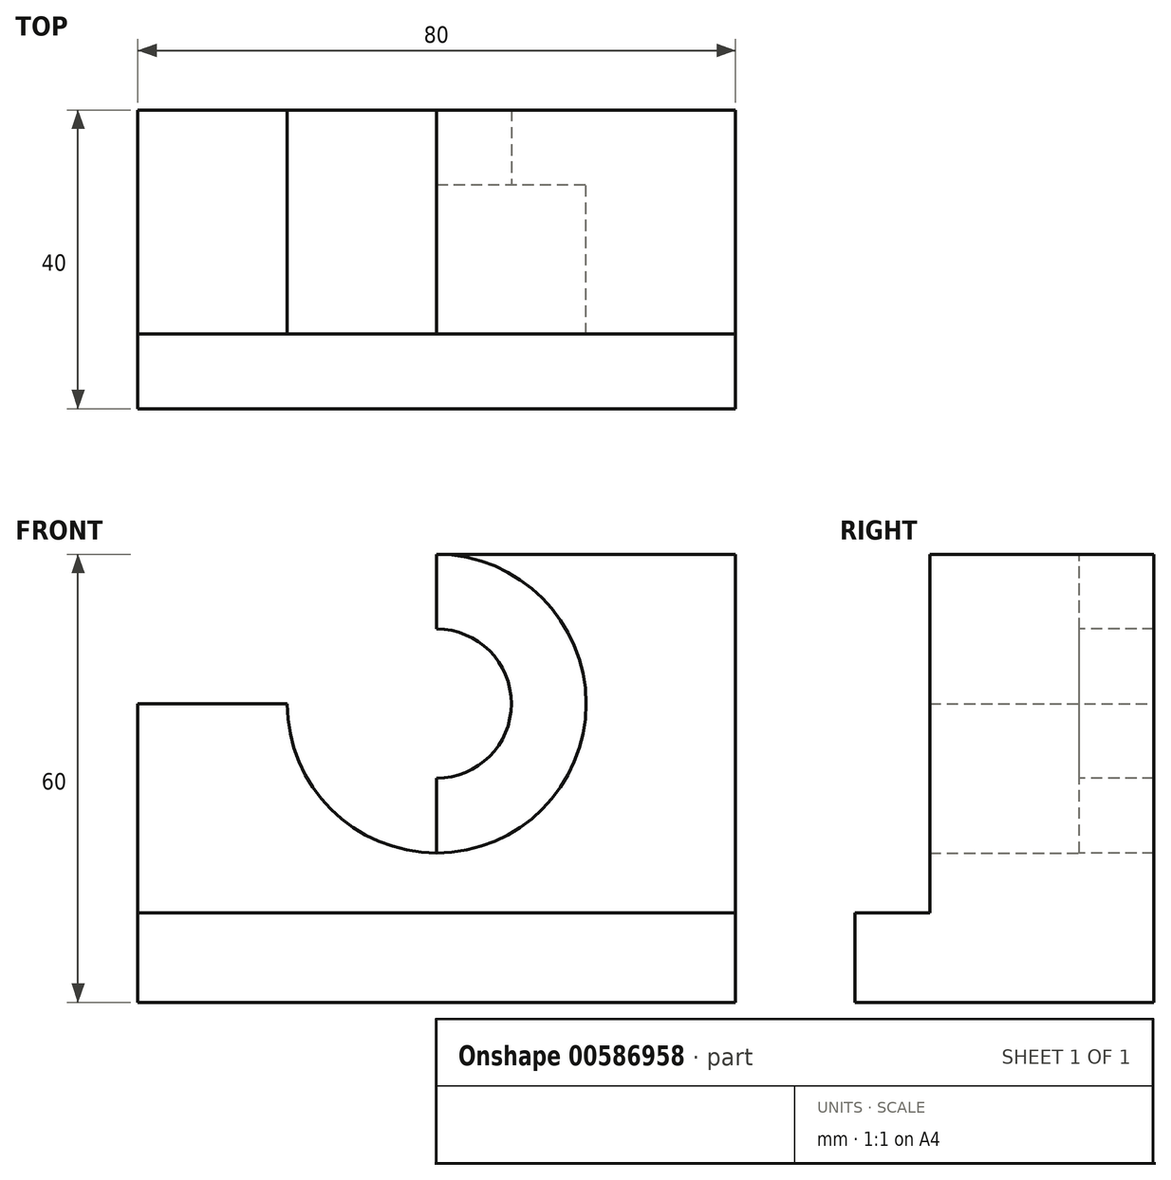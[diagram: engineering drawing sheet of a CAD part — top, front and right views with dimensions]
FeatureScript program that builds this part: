
annotation { "Feature Type Name" : "Feature", "Feature Type Description" : "" }
export const myFeature = defineFeature(function(context is Context, id is Id, definition is map)
    precondition{}
    {
        {
            var Q0;
            Q0=qCreatedBy(makeId("Top.planeOp"),FACE);
            var sketch = newSketch(context, id + "F0", { "sketchPlane" : qUnion([Q0])});
            skLineSegment(sketch, "E0.bottom", {"start": v(-24.56, -1) * mm, "end": v(55.44, -1) * mm});
            skLineSegment(sketch, "E0.top", {"start": v(-24.56, -41) * mm, "end": v(55.44, -41) * mm});
            skLineSegment(sketch, "E0.left", {"start": v(-24.56, -1) * mm, "end": v(-24.56, -41) * mm});
            skLineSegment(sketch, "E0.right", {"start": v(55.44, -1) * mm, "end": v(55.44, -41) * mm});
            skSolve(sketch);
        }
        {
            var Q0;
            Q0 = qSketchRegion(id + "F0", true);
            extrude(context, id + "F1", {"entities" : qUnion([Q0]), "depth" : 12 * mm, "offsetDistance" : 25 * mm});
        }
        {
            var Q0;
            Q0=makeQuery(id+"F1.opExtrude","CAP_FACE",FACE,{"disambiguationData":[OSD([sQuery(id+"F0.wireOp",EDGE,"E0.bottom"),sQuery(id+"F0.wireOp",EDGE,"E0.top"),sQuery(id+"F0.wireOp",EDGE,"E0.left"),sQuery(id+"F0.wireOp",EDGE,"E0.right")])],"isStart":false});
            var sketch = newSketch(context, id + "F2", { "sketchPlane" : qUnion([Q0])});
            skLineSegment(sketch, "E1", {"start": v(55.44, -1) * mm, "end": v(55.44, -11) * mm});
            skLineSegment(sketch, "E2", {"start": v(55.44, -11) * mm, "end": v(-24.56, -11) * mm});
            skSolve(sketch);
        }
        {
            var Q0;
            Q0 = qSketchRegion(id + "F2", true);
            var Q1;
            Q1=makeQuery(id+"F2.imprint","IMPRINT",FACE,{"disambiguationData":[TD([[makeQuery(id+"F2.imprint","IMPRINT",EDGE,{"derivedFrom":sQuery(id+"F2.wireOp",EDGE,"E1")}),-1.0]])]});
            extrude(context, id + "F3", {"entities" : qUnion([Q0, Q1]), "operationType" : NewBodyOperationType.ADD, "depth" : 48 * mm, "offsetDistance" : 25 * mm});
        }
        {
            var Q0;
            {var subQ0=sQuery(id+"F0.wireOp",EDGE,"E0.left");Q0=makeQuery(id+"F3.boolean.opBoolean","MERGE",FACE,{"derivedFrom":[makeQuery(id+"F1.opExtrude","SWEPT_FACE",FACE,{"disambiguationData":[OSD([subQ0])]}),makeQuery(id+"F3.opExtrude","SWEPT_FACE",FACE,{"disambiguationData":[OSD([subQ0])]})]});}
            var sketch = newSketch(context, id + "F4", { "sketchPlane" : qUnion([Q0])});
            skLineSegment(sketch, "E3", {"start": v(1, 0) * mm, "end": v(1, 40) * mm});
            skSolve(sketch);
        }
        {
            var Q0;
            {var subQ0=sQuery(id+"F0.wireOp",EDGE,"E0.bottom");Q0=makeQuery(id+"F3.boolean.opBoolean","MERGE",FACE,{"derivedFrom":[makeQuery(id+"F1.opExtrude","SWEPT_FACE",FACE,{"disambiguationData":[OSD([subQ0])]}),makeQuery(id+"F3.opExtrude","SWEPT_FACE",FACE,{"disambiguationData":[OSD([subQ0])]})]});}
            var sketch = newSketch(context, id + "F5", { "sketchPlane" : qUnion([Q0])});
            skLineSegment(sketch, "E4.0", {"start": v(24.56, 60) * mm, "end": v(24.56, 0) * mm});
            skLineSegment(sketch, "E5.0.0", {"start": v(24.56, 60) * mm, "end": v(24.56, 40) * mm});
            skLineSegment(sketch, "E5.0.1", {"start": v(24.56, 40) * mm, "end": v(24.56, 0) * mm});
            skLineSegment(sketch, "E5.0.3", {"start": v(24.56, 0) * mm, "end": v(24.56, 12) * mm});
            skLineSegment(sketch, "E5.0.5", {"start": v(24.56, 12) * mm, "end": v(24.56, 60) * mm});
            skLineSegment(sketch, "E6", {"start": v(24.56, 40) * mm, "end": v(-55.44, 40) * mm});
            skCircle(sketch, "E7", {"center": v(-15.44, 40) * mm, "radius": 20 * mm});
            skCircle(sketch, "E8", {"center": v(-15.44, 40) * mm, "radius": 10 * mm});
            skSolve(sketch);
        }
        {
            var Q0;
            {var subQ0=sQuery(id+"F5.wireOp",EDGE,"E7");var subQ1=sQuery(id+"F5.wireOp",EDGE,"E6");var subQ2=makeQuery(id+"F5.imprint","INTERSECT",VERTEX,{"disambiguationData":[OD(0.0)],"derivedFrom":[subQ1,subQ0]});Q0=makeQuery(id+"F5.imprint","IMPRINT",FACE,{"disambiguationData":[TD([[makeQuery(id+"F5.imprint","IMPRINT",EDGE,{"disambiguationData":[TD([[subQ2,-1.0]])],"derivedFrom":subQ1}),-1.0]])]});}
            var Q1;
            {var subQ0=sQuery(id+"F5.wireOp",EDGE,"E8");var subQ1=sQuery(id+"F5.wireOp",EDGE,"E6");var subQ2=makeQuery(id+"F5.imprint","INTERSECT",VERTEX,{"disambiguationData":[OD(0.0)],"derivedFrom":[subQ1,subQ0]});Q1=makeQuery(id+"F5.imprint","IMPRINT",FACE,{"disambiguationData":[TD([[makeQuery(id+"F5.imprint","IMPRINT",EDGE,{"disambiguationData":[TD([[subQ2,-1.0]])],"derivedFrom":subQ1}),-1.0]])]});}
            var Q2;
            {var subQ0=sQuery(id+"F5.wireOp",EDGE,"E8");var subQ1=sQuery(id+"F5.wireOp",EDGE,"E6");var subQ2=makeQuery(id+"F5.imprint","INTERSECT",VERTEX,{"disambiguationData":[OD(0.0)],"derivedFrom":[subQ1,subQ0]});Q2=makeQuery(id+"F5.imprint","IMPRINT",FACE,{"disambiguationData":[TD([[makeQuery(id+"F5.imprint","IMPRINT",EDGE,{"disambiguationData":[TD([[subQ2,-1.0]])],"derivedFrom":subQ1}),1.0]])]});}
            var Q3;
            {var subQ0=sQuery(id+"F5.wireOp",EDGE,"E7");var subQ1=sQuery(id+"F5.wireOp",EDGE,"E6");var subQ2=makeQuery(id+"F5.imprint","INTERSECT",VERTEX,{"disambiguationData":[OD(0.0)],"derivedFrom":[subQ1,subQ0]});Q3=makeQuery(id+"F5.imprint","IMPRINT",FACE,{"disambiguationData":[TD([[makeQuery(id+"F5.imprint","IMPRINT",EDGE,{"disambiguationData":[TD([[subQ2,-1.0]])],"derivedFrom":subQ1}),1.0]])]});}
            extrude(context, id + "F6", {"entities" : qUnion([Q0, Q1, Q2, Q3]), "operationType" : NewBodyOperationType.ADD, "oppositeDirection" : true, "depth" : 30 * mm, "offsetDistance" : 25 * mm});
        }
        {
            var Q0;
            Q0=makeQuery(id+"F6.opExtrude","CAP_FACE",FACE,{"disambiguationData":[OSD([sQuery(id+"F5.wireOp",EDGE,"E7")])],"isStart":false});
            var sketch = newSketch(context, id + "F7", { "sketchPlane" : qUnion([Q0])});
            skPoint(sketch, "E9.0", {"position": v(15.44, 40) * mm});
            skCircle(sketch, "E10.0", {"center": v(15.44, 40) * mm, "radius": 10 * mm});
            skSolve(sketch);
        }
        {
            var Q0;
            Q0 = qSketchRegion(id + "F7", true);
            extrude(context, id + "F8", {"entities" : qUnion([Q0]), "operationType" : NewBodyOperationType.REMOVE, "oppositeDirection" : true, "depth" : 282 * mm, "offsetDistance" : 25 * mm});
        }
        {
            var Q0;
            Q0=makeQuery(id+"F3.opExtrude","SWEPT_FACE",FACE,{"disambiguationData":[OSD([sQuery(id+"F2.wireOp",EDGE,"E2")])]});
            var sketch = newSketch(context, id + "F9", { "sketchPlane" : qUnion([Q0])});
            skLineSegment(sketch, "E11", {"start": v(23.58, 65.38) * mm, "end": v(55.44, 12) * mm});
            skLineSegment(sketch, "E12", {"start": v(15.44, 12) * mm, "end": v(15.44, 60) * mm});
            skLineSegment(sketch, "E13.MirrorCS", {"start": v(7.3, 65.38) * mm, "end": v(-24.56, 12) * mm});
            skSolve(sketch);
        }
        {
            var Q0;
            {var subQ1=sQuery(id+"F0.wireOp",EDGE,"E0.left");var subQ2=sQuery(id+"F2.wireOp",EDGE,"E2");var subQ8=makeQuery(id+"F3.opExtrude","SWEPT_EDGE",EDGE,{"disambiguationData":[OSD([subQ1,subQ2])]});Q0=makeQuery(id+"F9.imprint","IMPRINT",FACE,{"disambiguationData":[TD([[makeQuery(id+"F9.imprint","IMPRINT",EDGE,{"derivedFrom":subQ8}),1.0]])]});}
            var Q1;
            {var subQ1=sQuery(id+"F2.wireOp",EDGE,"E2");var subQ3=sQuery(id+"F2.wireOp",EDGE,"E1");var subQ5=sQuery(id+"F0.wireOp",EDGE,"E0.right");var subQ9=makeQuery(id+"F3.opExtrude","SWEPT_EDGE",EDGE,{"disambiguationData":[OSD([subQ5,subQ3,subQ1])]});Q1=makeQuery(id+"F9.imprint","IMPRINT",FACE,{"disambiguationData":[TD([[makeQuery(id+"F9.imprint","IMPRINT",EDGE,{"derivedFrom":subQ9}),-1.0]])]});}
            var Q2;
            {var subQ0=sQuery(id+"F9.wireOp",EDGE,"E13.MirrorCS");var subQ2=sQuery(id+"F2.wireOp",EDGE,"E2");var subQ3=makeQuery(id+"F3.opExtrude","SWEPT_FACE",FACE,{"disambiguationData":[OSD([subQ2])]});var subQ6=makeQuery(id+"F6.opExtrude","SWEPT_FACE",FACE,{"disambiguationData":[OSD([sQuery(id+"F5.wireOp",EDGE,"E7")])]});var subQ10=makeQuery(id+"F6.boolean.opBoolean","INTERSECT",EDGE,{"derivedFrom":[subQ3,subQ6]});var subQ11=makeQuery(id+"F9.imprint","INTERSECT",VERTEX,{"derivedFrom":[subQ10,subQ0]});Q2=makeQuery(id+"F9.imprint","IMPRINT",FACE,{"disambiguationData":[TD([[makeQuery(id+"F9.imprint","IMPRINT",EDGE,{"disambiguationData":[TD([[subQ11,1.0]])],"derivedFrom":subQ0}),1.0]])]});}
            var Q3;
            {var subQ0=sQuery(id+"F9.wireOp",EDGE,"E11");var subQ1=sQuery(id+"F2.wireOp",EDGE,"E2");var subQ2=makeQuery(id+"F3.opExtrude","SWEPT_FACE",FACE,{"disambiguationData":[OSD([subQ1])]});var subQ6=makeQuery(id+"F6.opExtrude","SWEPT_FACE",FACE,{"disambiguationData":[OSD([sQuery(id+"F5.wireOp",EDGE,"E7")])]});var subQ10=makeQuery(id+"F6.boolean.opBoolean","INTERSECT",EDGE,{"derivedFrom":[subQ2,subQ6]});var subQ11=makeQuery(id+"F9.imprint","INTERSECT",VERTEX,{"derivedFrom":[subQ10,subQ0]});Q3=makeQuery(id+"F9.imprint","IMPRINT",FACE,{"disambiguationData":[TD([[makeQuery(id+"F9.imprint","IMPRINT",EDGE,{"disambiguationData":[TD([[subQ11,1.0]])],"derivedFrom":subQ0}),-1.0]])]});}
            extrude(context, id + "F10", {"entities" : qUnion([Q0, Q1, Q2, Q3]), "operationType" : NewBodyOperationType.REMOVE, "oppositeDirection" : true, "depth" : 25 * mm, "offsetDistance" : 25 * mm});
        }
    });
